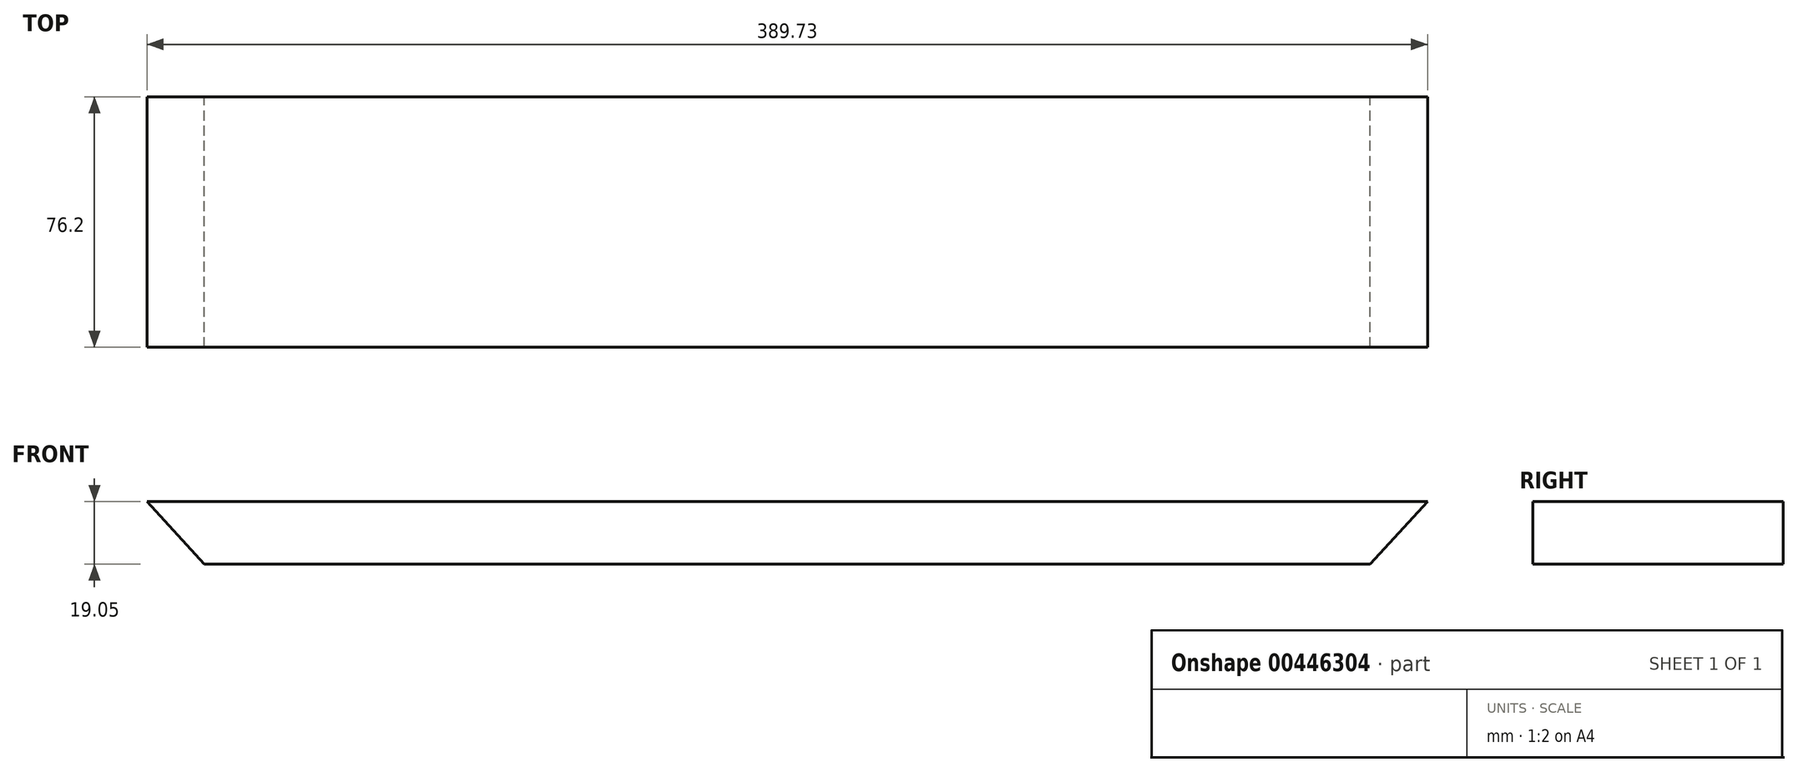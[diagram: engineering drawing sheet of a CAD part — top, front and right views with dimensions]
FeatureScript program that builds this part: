
annotation { "Feature Type Name" : "Feature", "Feature Type Description" : "" }
export const myFeature = defineFeature(function(context is Context, id is Id, definition is map)
    precondition{}
    {
        {
            var Q0;
            Q0=qCreatedBy(makeId("Front.planeOp"),FACE);
            var sketch = newSketch(context, id + "F0", { "sketchPlane" : qUnion([Q0])});
            skLineSegment(sketch, "E0", {"start": v(0, 0) * mm, "end": v(389.73, 0) * mm});
            skLineSegment(sketch, "E1", {"start": v(389.73, 0) * mm, "end": v(372.28, -19.05) * mm});
            skLineSegment(sketch, "E2", {"start": v(372.28, -19.05) * mm, "end": v(17.46, -19.05) * mm});
            skLineSegment(sketch, "E3", {"start": v(17.46, -19.05) * mm, "end": v(0, 0) * mm});
            skSolve(sketch);
        }
        {
            var Q0;
            Q0=makeQuery(id+"F0.imprint","IMPRINT",FACE,{"disambiguationData":[TD([[makeQuery(id+"F0.imprint","IMPRINT",EDGE,{"derivedFrom":sQuery(id+"F0.wireOp",EDGE,"E0")}),-1.0]])]});
            extrude(context, id + "F1", {"entities" : qUnion([Q0]), "depth" : 76.2 * mm});
        }
    });
